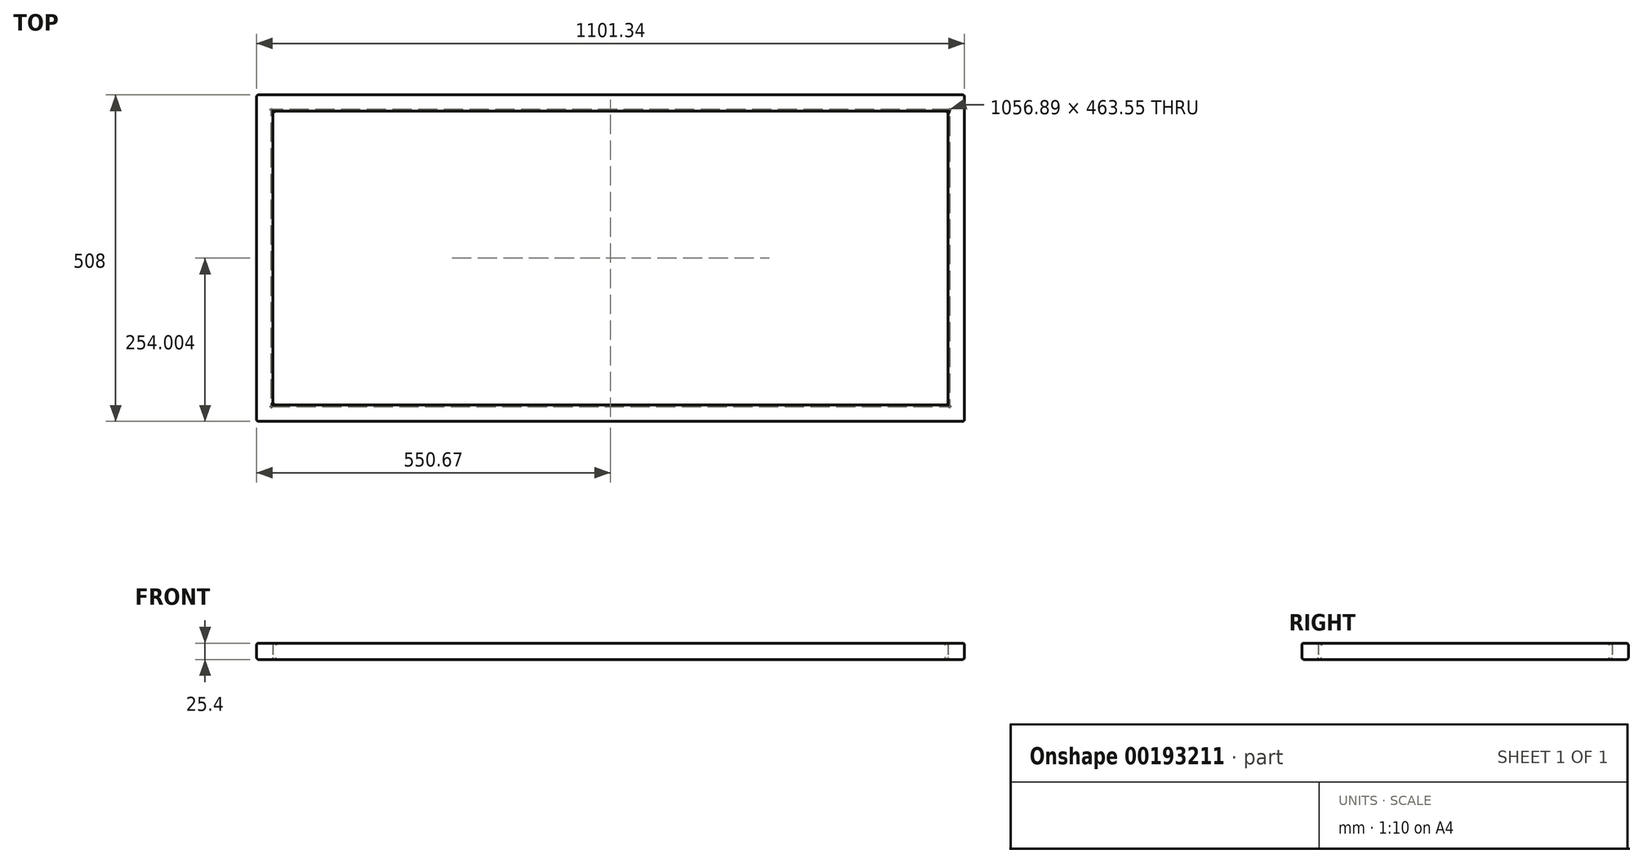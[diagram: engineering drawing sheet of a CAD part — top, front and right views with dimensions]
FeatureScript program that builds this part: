
annotation { "Feature Type Name" : "Feature", "Feature Type Description" : "" }
export const myFeature = defineFeature(function(context is Context, id is Id, definition is map)
    precondition{}
    {
        {
            var Q0;
            Q0=qCreatedBy(makeId("Top.planeOp"),FACE);
            var sketch = newSketch(context, id + "F0", { "sketchPlane" : qUnion([Q0])});
            skLineSegment(sketch, "E0.bottom", {"start": v(-277.3, 251.56) * mm, "end": v(824.04, 251.56) * mm});
            skLineSegment(sketch, "E0.top", {"start": v(-277.3, -256.44) * mm, "end": v(824.04, -256.44) * mm});
            skLineSegment(sketch, "E0.left", {"start": v(-277.3, 251.56) * mm, "end": v(-277.3, -256.44) * mm});
            skLineSegment(sketch, "E0.right", {"start": v(824.04, 251.56) * mm, "end": v(824.04, -256.44) * mm});
            skLineSegment(sketch, "E1.bottom", {"start": v(-251.9, 226.16) * mm, "end": v(798.64, 226.16) * mm});
            skLineSegment(sketch, "E1.top", {"start": v(-251.9, -231.04) * mm, "end": v(798.64, -231.04) * mm});
            skLineSegment(sketch, "E1.left", {"start": v(-251.9, 226.16) * mm, "end": v(-251.9, -231.04) * mm});
            skLineSegment(sketch, "E1.right", {"start": v(798.64, 226.16) * mm, "end": v(798.64, -231.04) * mm});
            skSolve(sketch);
        }
        {
            var Q0;
            Q0 = qSketchRegion(id + "F0", true);
            extrude(context, id + "F1", {"entities" : qUnion([Q0]), "depth" : 25.4 * mm});
        }
        {
            var Q0;
            Q0=makeQuery(id+"F1.opExtrude","CAP_EDGE",EDGE,{"disambiguationData":[OSD([sQuery(id+"F0.wireOp",EDGE,"E1.left")])],"isStart":false});
            var Q1;
            Q1=makeQuery(id+"F1.opExtrude","CAP_EDGE",EDGE,{"disambiguationData":[OSD([sQuery(id+"F0.wireOp",EDGE,"E1.bottom")])],"isStart":false});
            var Q2;
            Q2=makeQuery(id+"F1.opExtrude","CAP_EDGE",EDGE,{"disambiguationData":[OSD([sQuery(id+"F0.wireOp",EDGE,"E1.right")])],"isStart":false});
            var Q3;
            Q3=makeQuery(id+"F1.opExtrude","CAP_EDGE",EDGE,{"disambiguationData":[OSD([sQuery(id+"F0.wireOp",EDGE,"E1.top")])],"isStart":false});
            var Q4;
            Q4=makeQuery(id+"F1.opExtrude","CAP_EDGE",EDGE,{"disambiguationData":[OSD([sQuery(id+"F0.wireOp",EDGE,"E0.top")])],"isStart":false});
            var Q5;
            Q5=makeQuery(id+"F1.opExtrude","SWEPT_EDGE",EDGE,{"disambiguationData":[OSD([sQuery(id+"F0.wireOp",EDGE,"E0.top"),sQuery(id+"F0.wireOp",EDGE,"E0.right")])]});
            var Q6;
            Q6=makeQuery(id+"F1.opExtrude","CAP_EDGE",EDGE,{"disambiguationData":[OSD([sQuery(id+"F0.wireOp",EDGE,"E0.right")])],"isStart":false});
            var Q7;
            Q7=makeQuery(id+"F1.opExtrude","SWEPT_EDGE",EDGE,{"disambiguationData":[OSD([sQuery(id+"F0.wireOp",EDGE,"E0.bottom"),sQuery(id+"F0.wireOp",EDGE,"E0.right")])]});
            var Q8;
            Q8=makeQuery(id+"F1.opExtrude","CAP_EDGE",EDGE,{"disambiguationData":[OSD([sQuery(id+"F0.wireOp",EDGE,"E0.bottom")])],"isStart":false});
            var Q9;
            Q9=makeQuery(id+"F1.opExtrude","CAP_EDGE",EDGE,{"disambiguationData":[OSD([sQuery(id+"F0.wireOp",EDGE,"E0.left")])],"isStart":false});
            var Q10;
            Q10=makeQuery(id+"F1.opExtrude","SWEPT_EDGE",EDGE,{"disambiguationData":[OSD([sQuery(id+"F0.wireOp",EDGE,"E0.top"),sQuery(id+"F0.wireOp",EDGE,"E0.left")])]});
            var Q11;
            Q11=makeQuery(id+"F1.opExtrude","CAP_EDGE",EDGE,{"disambiguationData":[OSD([sQuery(id+"F0.wireOp",EDGE,"E0.bottom")])],"isStart":true});
            var Q12;
            Q12=makeQuery(id+"F1.opExtrude","CAP_EDGE",EDGE,{"disambiguationData":[OSD([sQuery(id+"F0.wireOp",EDGE,"E0.right")])],"isStart":true});
            var Q13;
            Q13=makeQuery(id+"F1.opExtrude","CAP_EDGE",EDGE,{"disambiguationData":[OSD([sQuery(id+"F0.wireOp",EDGE,"E1.top")])],"isStart":true});
            var Q14;
            Q14=makeQuery(id+"F1.opExtrude","CAP_EDGE",EDGE,{"disambiguationData":[OSD([sQuery(id+"F0.wireOp",EDGE,"E1.left")])],"isStart":true});
            var Q15;
            Q15=makeQuery(id+"F1.opExtrude","SWEPT_EDGE",EDGE,{"disambiguationData":[OSD([sQuery(id+"F0.wireOp",EDGE,"E0.bottom"),sQuery(id+"F0.wireOp",EDGE,"E0.left")])]});
            var Q16;
            Q16=makeQuery(id+"F1.opExtrude","CAP_EDGE",EDGE,{"disambiguationData":[OSD([sQuery(id+"F0.wireOp",EDGE,"E1.right")])],"isStart":true});
            var Q17;
            Q17=makeQuery(id+"F1.opExtrude","CAP_EDGE",EDGE,{"disambiguationData":[OSD([sQuery(id+"F0.wireOp",EDGE,"E1.bottom")])],"isStart":true});
            var Q18;
            Q18=makeQuery(id+"F1.opExtrude","CAP_EDGE",EDGE,{"disambiguationData":[OSD([sQuery(id+"F0.wireOp",EDGE,"E0.left")])],"isStart":true});
            var Q19;
            Q19=makeQuery(id+"F1.opExtrude","CAP_EDGE",EDGE,{"disambiguationData":[OSD([sQuery(id+"F0.wireOp",EDGE,"E0.top")])],"isStart":true});
            fillet(context, id + "F2", {"entities" : qUnion([Q0, Q1, Q2, Q3, Q4, Q5, Q6, Q7, Q8, Q9, Q10, Q11, Q12, Q13, Q14, Q15, Q16, Q17, Q18, Q19]), "radius" : 3.17 * mm, "tangentPropagation" : true, "allowEdgeOverflow" : false});
        }
        {
            var Q0;
            Q0=makeQuery(id+"F1.opExtrude","SWEPT_EDGE",EDGE,{"disambiguationData":[OSD([sQuery(id+"F0.wireOp",EDGE,"E1.top"),sQuery(id+"F0.wireOp",EDGE,"E1.left")])]});
            var Q1;
            Q1=makeQuery(id+"F1.opExtrude","SWEPT_EDGE",EDGE,{"disambiguationData":[OSD([sQuery(id+"F0.wireOp",EDGE,"E1.top"),sQuery(id+"F0.wireOp",EDGE,"E1.right")])]});
            var Q2;
            Q2=makeQuery(id+"F1.opExtrude","SWEPT_EDGE",EDGE,{"disambiguationData":[OSD([sQuery(id+"F0.wireOp",EDGE,"E1.bottom"),sQuery(id+"F0.wireOp",EDGE,"E1.right")])]});
            var Q3;
            Q3=makeQuery(id+"F1.opExtrude","SWEPT_EDGE",EDGE,{"disambiguationData":[OSD([sQuery(id+"F0.wireOp",EDGE,"E1.bottom"),sQuery(id+"F0.wireOp",EDGE,"E1.left")])]});
            fillet(context, id + "F3", {"entities" : qUnion([Q0, Q1, Q2, Q3]), "radius" : 5.08 * mm, "tangentPropagation" : true, "allowEdgeOverflow" : false});
        }
    });
